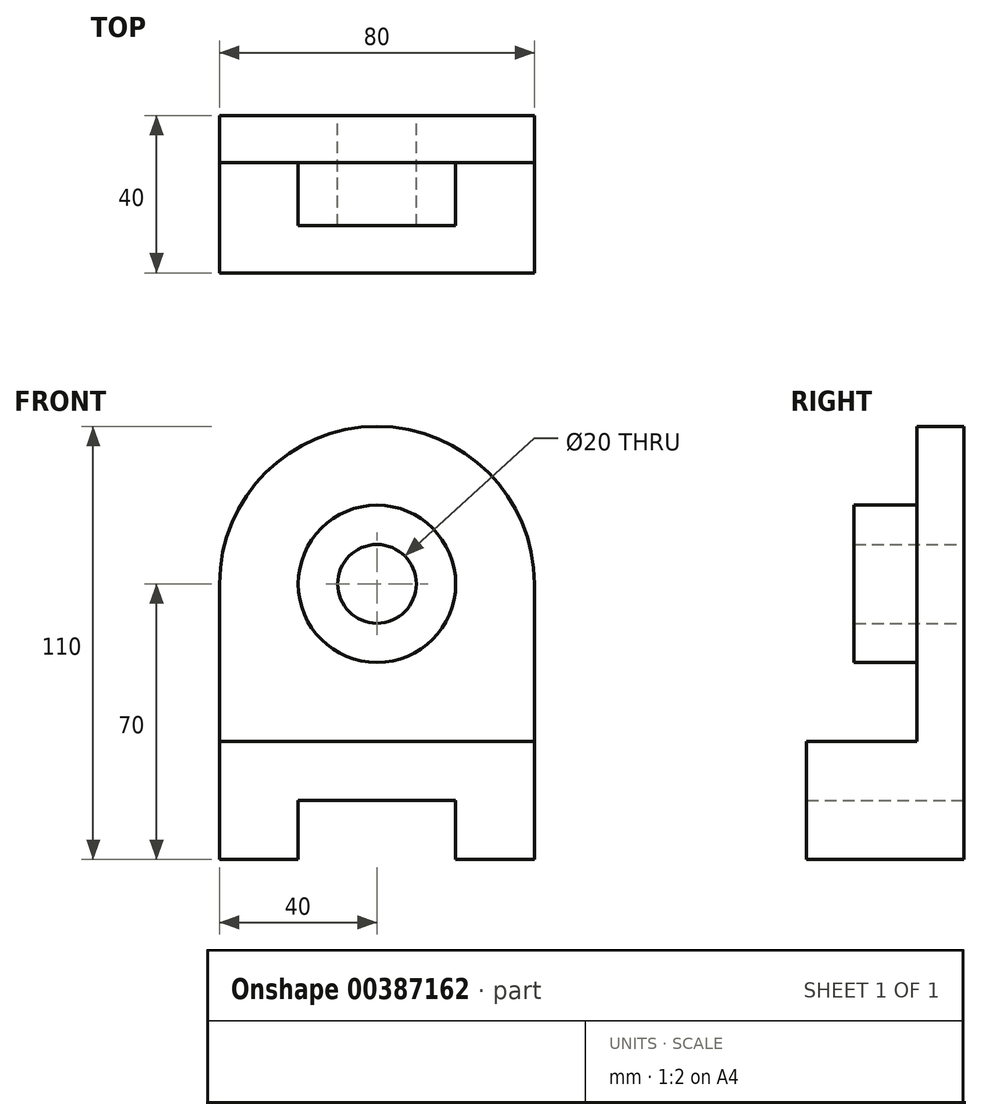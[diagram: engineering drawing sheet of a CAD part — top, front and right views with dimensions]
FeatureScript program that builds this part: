
annotation { "Feature Type Name" : "Feature", "Feature Type Description" : "" }
export const myFeature = defineFeature(function(context is Context, id is Id, definition is map)
    precondition{}
    {
        {
            var Q0;
            Q0=qCreatedBy(makeId("Front.planeOp"),FACE);
            var sketch = newSketch(context, id + "F0", { "sketchPlane" : qUnion([Q0])});
            skCircle(sketch, "E0", {"center": v(0, 0) * mm, "radius": 40 * mm});
            skCircle(sketch, "E1", {"center": v(0, 0) * mm, "radius": 20 * mm});
            skCircle(sketch, "E2", {"center": v(0, 0) * mm, "radius": 10 * mm});
            skLineSegment(sketch, "E3", {"start": v(-40, 0) * mm, "end": v(-40, -70) * mm});
            skLineSegment(sketch, "E4", {"start": v(-40, -70) * mm, "end": v(-20, -70) * mm});
            skLineSegment(sketch, "E5", {"start": v(-20, -70) * mm, "end": v(-20, -55) * mm});
            skLineSegment(sketch, "E6", {"start": v(-20, -55) * mm, "end": v(20, -55) * mm});
            skLineSegment(sketch, "E7", {"start": v(20, -55) * mm, "end": v(20, -70) * mm});
            skLineSegment(sketch, "E8", {"start": v(20, -70) * mm, "end": v(40, -70) * mm});
            skLineSegment(sketch, "E9", {"start": v(40, -70) * mm, "end": v(40, 0) * mm});
            skLineSegment(sketch, "E10", {"start": v(0, -40) * mm, "end": v(40, -40) * mm});
            skLineSegment(sketch, "E11", {"start": v(40, -40) * mm, "end": v(-40, -40) * mm});
            skSolve(sketch);
        }
        {
            var Q0;
            Q0=makeQuery(id+"F0.imprint","IMPRINT",FACE,{"disambiguationData":[TD([[makeQuery(id+"F0.imprint","IMPRINT",EDGE,{"derivedFrom":sQuery(id+"F0.wireOp",EDGE,"E1")}),1.0]])]});
            extrude(context, id + "F1", {"entities" : qUnion([Q0]), "depth" : 28 * mm});
        }
        {
            var Q0;
            {var subQ0=sQuery(id+"F0.wireOp",EDGE,"E4");Q0=makeQuery(id+"F0.imprint","IMPRINT",FACE,{"disambiguationData":[TD([[makeQuery(id+"F0.imprint","IMPRINT",EDGE,{"derivedFrom":subQ0}),1.0]])]});}
            extrude(context, id + "F2", {"entities" : qUnion([Q0]), "depth" : 40 * mm});
        }
        {
            var Q0;
            Q0=makeQuery(id+"F0.imprint","IMPRINT",FACE,{"disambiguationData":[TD([[makeQuery(id+"F0.imprint","IMPRINT",EDGE,{"derivedFrom":sQuery(id+"F0.wireOp",EDGE,"E1")}),-1.0]])]});
            var Q1;
            {var subQ0=sQuery(id+"F0.wireOp",EDGE,"E3");var subQ1=sQuery(id+"F0.wireOp",EDGE,"E0");var subQ2=makeQuery(id+"F0.imprint","INTERSECT",VERTEX,{"derivedFrom":[subQ1,subQ0]});Q1=makeQuery(id+"F0.imprint","IMPRINT",FACE,{"disambiguationData":[TD([[makeQuery(id+"F0.imprint","IMPRINT",EDGE,{"disambiguationData":[TD([[subQ2,-1.0]])],"derivedFrom":subQ1}),-1.0]])]});}
            var Q2;
            {var subQ0=sQuery(id+"F0.wireOp",EDGE,"E9");var subQ1=sQuery(id+"F0.wireOp",EDGE,"E0");var subQ2=makeQuery(id+"F0.imprint","INTERSECT",VERTEX,{"derivedFrom":[subQ1,subQ0]});Q2=makeQuery(id+"F0.imprint","IMPRINT",FACE,{"disambiguationData":[TD([[makeQuery(id+"F0.imprint","IMPRINT",EDGE,{"disambiguationData":[TD([[subQ2,1.0]])],"derivedFrom":subQ1}),-1.0]])]});}
            extrude(context, id + "F3", {"entities" : qUnion([Q0, Q1, Q2]), "operationType" : NewBodyOperationType.ADD, "depth" : 12 * mm});
        }
    });
